# Revit family: Shower-Handshower-KOHLER-SHIFT-K-10257T
name_source: partatom
category: Plumbing Fixtures
revit_build: Autodesk Revit 2017 (Build: 20160225_1515(x64)
units: mm (PartAtom-declared; Revit-internal decimal feet)

## family parameters
Cut with Voids When Loaded = No
Host = Face
OmniClass Number = 23.31.17.00
OmniClass Title = Showers
Part Type = Normal
Room Calculation Point = No
Round Connector Dimension = Use Diameter
Shared = No

## types (4) — shared parameters
ADA Compliant = No
Assembly Code = D2010700
CW Connection = No
Cold Water Inlet = Cold Water Inlet
Date Modified = 04/23/2021
Default Elevation = 0"
Description = STICK HANDSHOWER W/BLACK HANDLE
Drain Included = No
Flow Rate = 0 GPM
HW Connection = Yes
Height = 9"
Hot Water Inlet = Hot Water Inlet
Length = 15/16"
Manufacturer = KOHLER Co.
Master Format 2014 = 22 42 23
Master Format 2014 Name = Residential Showers
Material = Premium Metal Construction
Pressure = 0.00 psi
Product Name = SHIFT
Tempered Water Inlet = Tempered Water Inlet
URL = http://www.kohler.com.cn
Vent Connection = No
Waste Connection = No
Waste Water Outlet = Waste Water Outlet
WaterSense Certified = No
Width = 1 1/8"

## per-type parameters (varying)
| type | Finish | Metallic Handle | Model | Plastic Handle | Type |
| CP-Polished Chrome | Kohler-Metal-CP-Polished_Chrome | No | K-10257T-CP | Yes | 1 |
| PGD-Eternal Gold | Kohler-Metal-PGD-Eternal_Gold | No | K-10257T-PGD | Yes | 2 |
| SN-Champagne Gold | Kohler-Metal-SN-Champagne_Gold | No | K-10257T-SN | Yes | 3 |
| A-CP-Polished Chrome | Kohler-Metal-CP-Polished_Chrome | Yes | K-10257T-A-CP | No | 4 |

## geometry (parser evidence)
native form markers: Sweep x5
no freeform markers — native parametric forms only
